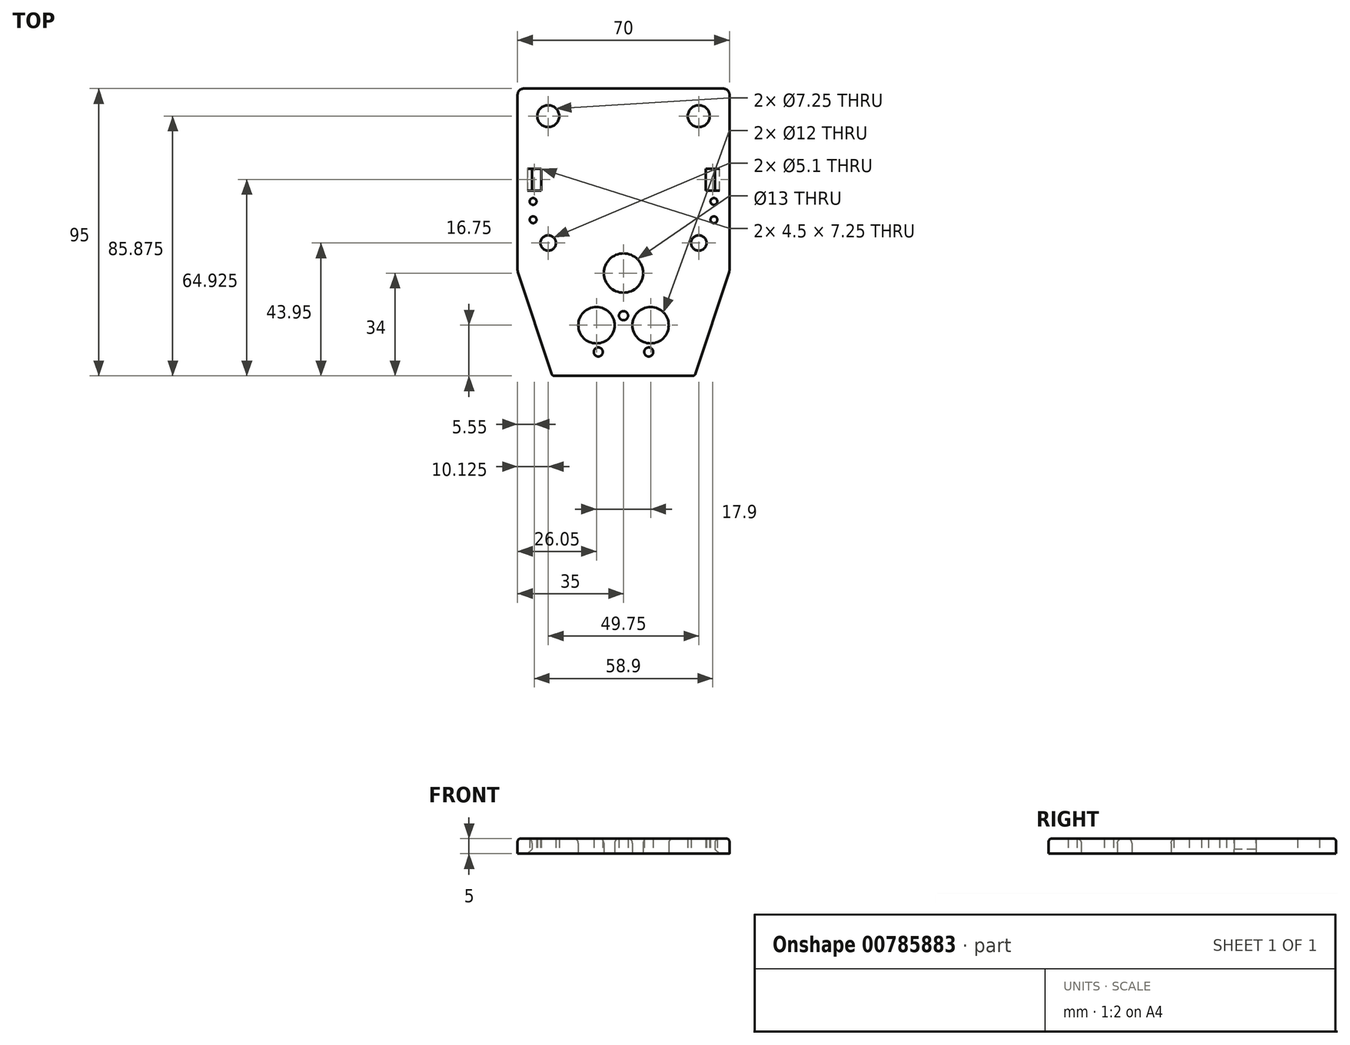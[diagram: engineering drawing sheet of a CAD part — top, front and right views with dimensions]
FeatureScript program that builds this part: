
annotation { "Feature Type Name" : "Feature", "Feature Type Description" : "" }
export const myFeature = defineFeature(function(context is Context, id is Id, definition is map)
    precondition{}
    {
        {
            var Q0;
            Q0=qCreatedBy(makeId("Top.planeOp"),FACE);
            var sketch = newSketch(context, id + "F0", { "sketchPlane" : qUnion([Q0])});
            skLineSegment(sketch, "E0.bottom", {"start": v(0, 31.98) * mm, "end": v(-33, 31.98) * mm});
            skLineSegment(sketch, "E0.right", {"start": v(-35, 29.98) * mm, "end": v(-35, 0) * mm});
            skLineSegment(sketch, "E1.MirrorCS", {"start": v(-35, -28.02) * mm, "end": v(-35, 0) * mm});
            skLineSegment(sketch, "E2.MirrorCS", {"start": v(0, 31.98) * mm, "end": v(33, 31.98) * mm});
            skLineSegment(sketch, "E3.MirrorCS", {"start": v(35, 29.98) * mm, "end": v(35, 0) * mm});
            skLineSegment(sketch, "E4.MirrorCS", {"start": v(35, -28.02) * mm, "end": v(35, 0) * mm});
            skCircle(sketch, "E5", {"center": v(24.87, 22.86) * mm, "radius": 3.62 * mm});
            skCircle(sketch, "E6.MirrorC", {"center": v(-24.87, 22.86) * mm, "radius": 3.62 * mm});
            skCircle(sketch, "E7", {"center": v(29.88, -5.34) * mm, "radius": 1.13 * mm});
            skCircle(sketch, "E8", {"center": v(29.88, -11.4) * mm, "radius": 1.13 * mm});
            skCircle(sketch, "E9.MirrorC", {"center": v(-29.88, -5.34) * mm, "radius": 1.13 * mm});
            skCircle(sketch, "E10.MirrorC", {"center": v(-29.88, -11.4) * mm, "radius": 1.13 * mm});
            skPoint(sketch, "E11.visualSharp", {"position": v(-35, 31.98) * mm});
            skArc(sketch, "E11.filletArc", {"start": v(-33, 31.98) * mm, "mid": v(-34.41, 31.4) * mm, "end": v(-35, 29.98) * mm});
            skPoint(sketch, "E12.visualSharp", {"position": v(35, 31.98) * mm});
            skArc(sketch, "E12.filletArc", {"start": v(35, 29.98) * mm, "mid": v(34.41, 31.4) * mm, "end": v(33, 31.98) * mm});
            skLineSegment(sketch, "E13.top", {"start": v(-23.56, -63.02) * mm, "end": v(0, -63.02) * mm});
            skLineSegment(sketch, "E14", {"start": v(-23.56, -63.02) * mm, "end": v(-34.9, -28.65) * mm});
            skLineSegment(sketch, "E15.MirrorCS", {"start": v(23.56, -63.02) * mm, "end": v(0, -63.02) * mm});
            skLineSegment(sketch, "E16.MirrorCS", {"start": v(23.56, -63.02) * mm, "end": v(34.9, -28.65) * mm});
            skPoint(sketch, "E17.visualSharp", {"position": v(-35, -28.34) * mm});
            skArc(sketch, "E17.filletArc", {"start": v(-35, -28.02) * mm, "mid": v(-34.97, -28.34) * mm, "end": v(-34.9, -28.65) * mm});
            skPoint(sketch, "E18.visualSharp", {"position": v(35, -28.34) * mm});
            skArc(sketch, "E18.filletArc", {"start": v(34.9, -28.65) * mm, "mid": v(34.97, -28.34) * mm, "end": v(35, -28.02) * mm});
            skCircle(sketch, "E19", {"center": v(0, -29.02) * mm, "radius": 6.5 * mm});
            skCircle(sketch, "E20", {"center": v(8.95, -46.27) * mm, "radius": 6 * mm});
            skCircle(sketch, "E21.MirrorC", {"center": v(-8.95, -46.27) * mm, "radius": 6 * mm});
            skCircle(sketch, "E22", {"center": v(0, -43.12) * mm, "radius": 1.5 * mm});
            skCircle(sketch, "E23", {"center": v(8.33, -55.12) * mm, "radius": 1.5 * mm});
            skCircle(sketch, "E24.MirrorC", {"center": v(-8.33, -55.12) * mm, "radius": 1.5 * mm});
            skLineSegment(sketch, "E25.bottom", {"start": v(27.2, 5.53) * mm, "end": v(30.2, 5.53) * mm});
            skLineSegment(sketch, "E25.top", {"start": v(27.2, -1.72) * mm, "end": v(30.2, -1.72) * mm});
            skLineSegment(sketch, "E25.left", {"start": v(27.2, 5.53) * mm, "end": v(27.2, -1.72) * mm});
            skLineSegment(sketch, "E25.right", {"start": v(30.2, 5.53) * mm, "end": v(30.2, -1.72) * mm});
            skLineSegment(sketch, "E26.MirrorCS", {"start": v(-27.2, -1.72) * mm, "end": v(-30.2, -1.72) * mm});
            skLineSegment(sketch, "E27.MirrorCS", {"start": v(-27.2, 5.53) * mm, "end": v(-27.2, -1.72) * mm});
            skLineSegment(sketch, "E28.MirrorCS", {"start": v(-27.2, 5.53) * mm, "end": v(-30.2, 5.53) * mm});
            skLineSegment(sketch, "E29.MirrorCS", {"start": v(-30.2, 5.53) * mm, "end": v(-30.2, -1.72) * mm});
            skCircle(sketch, "E30", {"center": v(-24.87, -19.07) * mm, "radius": 2.55 * mm});
            skCircle(sketch, "E31.MirrorC", {"center": v(24.87, -19.07) * mm, "radius": 2.55 * mm});
            skLineSegment(sketch, "E32", {"start": v(35, -28.02) * mm, "end": v(-35, -28.02) * mm, "construction": true});
            skEllipse(sketch, "E33", {"center": v(15.03, -28.02) * mm, "majorRadius": 9 * mm, "minorRadius": 4.5 * mm, "majorAxis": v(0.41, -0.91), "construction": true});
            skEllipse(sketch, "E34.MirrorC", {"center": v(-15.03, -28.02) * mm, "majorRadius": 9 * mm, "minorRadius": 4.5 * mm, "majorAxis": v(-0.41, -0.91), "construction": true});
            skSolve(sketch);
        }
        {
            var Q0;
            Q0=makeQuery(id+"F0.imprint","IMPRINT",FACE,{"disambiguationData":[TD([[makeQuery(id+"F0.imprint","IMPRINT",EDGE,{"derivedFrom":sQuery(id+"F0.wireOp",EDGE,"E0.bottom")}),1.0]])]});
            extrude(context, id + "F1", {"entities" : qUnion([Q0]), "depth" : 5 * mm, "offsetDistance" : 25 * mm});
        }
        {
            var Q0;
            Q0=makeQuery(id+"F1.opExtrude","CAP_EDGE",EDGE,{"disambiguationData":[OSD([sQuery(id+"F0.wireOp",EDGE,"E25.right")])],"isStart":false});
            fillet(context, id + "F2", {"entities" : qUnion([Q0]), "radius" : 1.5 * mm, "tangentPropagation" : true, "allowEdgeOverflow" : false});
        }
        {
            var Q0;
            Q0=makeQuery(id+"F1.opExtrude","CAP_EDGE",EDGE,{"disambiguationData":[OSD([sQuery(id+"F0.wireOp",EDGE,"E29.MirrorCS")])],"isStart":false});
            fillet(context, id + "F3", {"entities" : qUnion([Q0]), "radius" : 1.5 * mm, "tangentPropagation" : true, "allowEdgeOverflow" : false});
        }
        {
            var Q0;
            Q0=makeQuery(id+"F1.opExtrude","CAP_EDGE",EDGE,{"disambiguationData":[OSD([sQuery(id+"F0.wireOp",EDGE,"E25.right")])],"isStart":true});
            chamfer(context, id + "F4", {"entities" : qUnion([Q0]), "width" : 1.5 * mm, "tangentPropagation" : true});
        }
        {
            var Q0;
            Q0=makeQuery(id+"F1.opExtrude","CAP_EDGE",EDGE,{"disambiguationData":[OSD([sQuery(id+"F0.wireOp",EDGE,"E29.MirrorCS")])],"isStart":true});
            chamfer(context, id + "F5", {"entities" : qUnion([Q0]), "width" : 1.5 * mm, "tangentPropagation" : true});
        }
        {
            var Q0;
            Q0=makeQuery(id+"F1.opExtrude","CAP_EDGE",EDGE,{"disambiguationData":[OSD([sQuery(id+"F0.wireOp",EDGE,"E19")])],"isStart":false});
            var Q1;
            Q1=makeQuery(id+"F1.opExtrude","CAP_EDGE",EDGE,{"disambiguationData":[OSD([sQuery(id+"F0.wireOp",EDGE,"E21.MirrorC")])],"isStart":false});
            var Q2;
            Q2=makeQuery(id+"F1.opExtrude","CAP_EDGE",EDGE,{"disambiguationData":[OSD([sQuery(id+"F0.wireOp",EDGE,"E20")])],"isStart":false});
            fillet(context, id + "F6", {"entities" : qUnion([Q0, Q1, Q2]), "radius" : 1.5 * mm, "tangentPropagation" : true, "allowEdgeOverflow" : false});
        }
        {
            var Q0;
            Q0=makeQuery(id+"F1.opExtrude","CAP_EDGE",EDGE,{"disambiguationData":[OSD([sQuery(id+"F0.wireOp",EDGE,"E16.MirrorCS")])],"isStart":false});
            var Q1;
            Q1=makeQuery(id+"F1.opExtrude","CAP_EDGE",EDGE,{"disambiguationData":[OSD([sQuery(id+"F0.wireOp",EDGE,"E13.top"),sQuery(id+"F0.wireOp",EDGE,"E15.MirrorCS")])],"isStart":false});
            var Q2;
            Q2=makeQuery(id+"F1.opExtrude","SWEPT_EDGE",EDGE,{"disambiguationData":[OSD([sQuery(id+"F0.wireOp",EDGE,"E15.MirrorCS"),sQuery(id+"F0.wireOp",EDGE,"E16.MirrorCS")])]});
            var Q3;
            Q3=makeQuery(id+"F1.opExtrude","SWEPT_EDGE",EDGE,{"disambiguationData":[OSD([sQuery(id+"F0.wireOp",EDGE,"E13.top"),sQuery(id+"F0.wireOp",EDGE,"E14")])]});
            var Q4;
            Q4=makeQuery(id+"F1.opExtrude","CAP_EDGE",EDGE,{"disambiguationData":[OSD([sQuery(id+"F0.wireOp",EDGE,"E18.filletArc")])],"isStart":false});
            var Q5;
            Q5=makeQuery(id+"F1.opExtrude","CAP_EDGE",EDGE,{"disambiguationData":[OSD([sQuery(id+"F0.wireOp",EDGE,"E17.filletArc")])],"isStart":false});
            fillet(context, id + "F7", {"entities" : qUnion([Q0, Q1, Q2, Q3, Q4, Q5]), "radius" : 1 * mm, "tangentPropagation" : true, "allowEdgeOverflow" : false});
        }
    });
